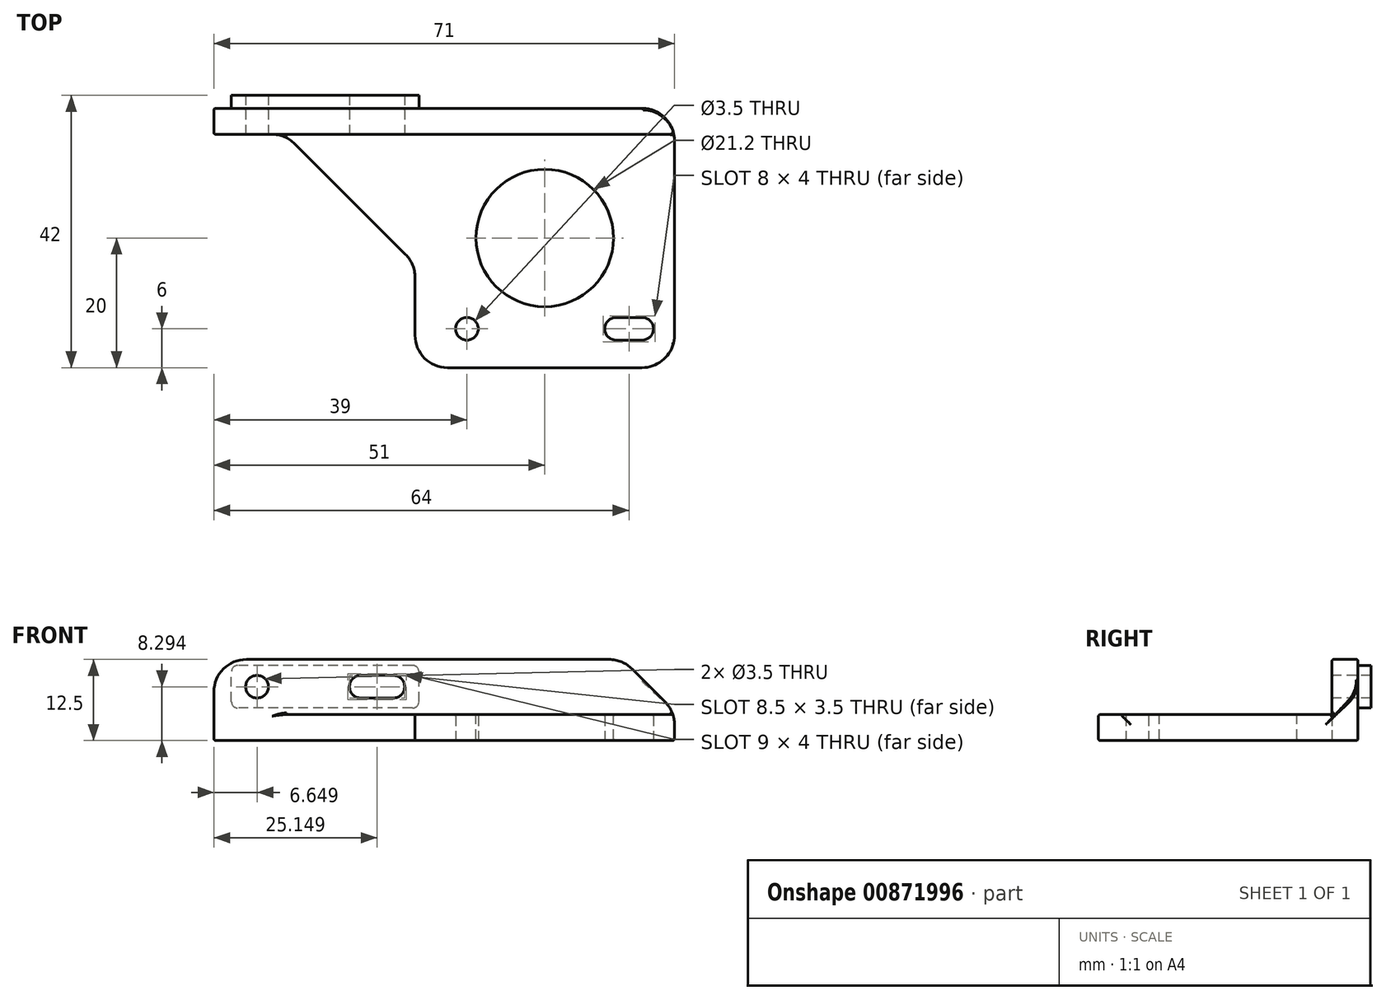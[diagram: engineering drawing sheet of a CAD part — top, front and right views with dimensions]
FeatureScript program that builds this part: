
annotation { "Feature Type Name" : "Feature", "Feature Type Description" : "" }
export const myFeature = defineFeature(function(context is Context, id is Id, definition is map)
    precondition{}
    {
        {
            var Q0;
            Q0=qCreatedBy(makeId("Top.planeOp"),FACE);
            var sketch = newSketch(context, id + "F0", { "sketchPlane" : qUnion([Q0])});
            skLineSegment(sketch, "E0.bottom", {"start": v(20, -20) * mm, "end": v(-20, -20) * mm});
            skLineSegment(sketch, "E0.top", {"start": v(20, 20) * mm, "end": v(-20, 20) * mm});
            skLineSegment(sketch, "E0.left", {"start": v(20, -20) * mm, "end": v(20, 20) * mm});
            skLineSegment(sketch, "E0.right", {"start": v(-20, -20) * mm, "end": v(-20, 20) * mm});
            skPoint(sketch, "E0.middle", {"position": v(0, 0) * mm});
            skCircle(sketch, "E1", {"center": v(-12, -14) * mm, "radius": 1.75 * mm});
            skLineSegment(sketch, "E2", {"start": v(11, -14) * mm, "end": v(15, -14) * mm});
            skArc(sketch, "E3.0.startCap", {"start": v(11, -15.75) * mm, "mid": v(9.25, -14) * mm, "end": v(11, -12.25) * mm});
            skArc(sketch, "E3.0.endCap", {"start": v(15, -12.25) * mm, "mid": v(16.75, -14) * mm, "end": v(15, -15.75) * mm});
            skLineSegment(sketch, "E3.0.left", {"start": v(11, -12.25) * mm, "end": v(15, -12.25) * mm});
            skLineSegment(sketch, "E3.0.right", {"start": v(11, -15.75) * mm, "end": v(15, -15.75) * mm});
            skSolve(sketch);
        }
        {
            var Q0;
            Q0 = qSketchRegion(id + "F0", true);
            extrude(context, id + "F1", {"entities" : qUnion([Q0]), "depth" : 4 * mm, "offsetDistance" : 25 * mm});
        }
        {
            var Q0;
            Q0=qCreatedBy(makeId("Top.planeOp"),FACE);
            var sketch = newSketch(context, id + "F2", { "sketchPlane" : qUnion([Q0])});
            skLineSegment(sketch, "E4.0", {"start": v(20, 20) * mm, "end": v(-20, 20) * mm, "construction": true});
            skLineSegment(sketch, "E5.bottom", {"start": v(20, 20) * mm, "end": v(-51, 20) * mm});
            skLineSegment(sketch, "E5.top", {"start": v(20, 16) * mm, "end": v(-51, 16) * mm});
            skLineSegment(sketch, "E5.left", {"start": v(20, 20) * mm, "end": v(20, 16) * mm});
            skLineSegment(sketch, "E5.right", {"start": v(-51, 20) * mm, "end": v(-51, 16) * mm});
            skSolve(sketch);
        }
        {
            var Q0;
            Q0 = qSketchRegion(id + "F2", true);
            extrude(context, id + "F3", {"entities" : qUnion([Q0]), "operationType" : NewBodyOperationType.ADD, "depth" : 12.5 * mm, "offsetDistance" : 25 * mm});
        }
        {
            var Q0;
            Q0=makeQuery(id+"F3.opExtrude","CAP_EDGE",EDGE,{"disambiguationData":[OSD([sQuery(id+"F2.wireOp",EDGE,"E5.left")])],"isStart":false});
            chamfer(context, id + "F4", {"entities" : qUnion([Q0]), "width" : 8 * mm, "tangentPropagation" : true});
        }
        {
            var Q0;
            Q0=makeQuery(id+"F3.opExtrude","SWEPT_FACE",FACE,{"disambiguationData":[OSD([sQuery(id+"F2.wireOp",EDGE,"E5.top")])]});
            var sketch = newSketch(context, id + "F5", { "sketchPlane" : qUnion([Q0])});
            skCircle(sketch, "E6", {"center": v(-44.35, 8.3) * mm, "radius": 1.75 * mm});
            skLineSegment(sketch, "E7", {"start": v(-28.35, 8.3) * mm, "end": v(-23.35, 8.3) * mm});
            skArc(sketch, "E8.0.startCap", {"start": v(-28.35, 6.54) * mm, "mid": v(-30.1, 8.3) * mm, "end": v(-28.35, 10.04) * mm});
            skArc(sketch, "E8.0.endCap", {"start": v(-23.35, 10.04) * mm, "mid": v(-21.6, 8.3) * mm, "end": v(-23.35, 6.54) * mm});
            skLineSegment(sketch, "E8.0.left", {"start": v(-28.35, 10.04) * mm, "end": v(-23.35, 10.04) * mm});
            skLineSegment(sketch, "E8.0.right", {"start": v(-28.35, 6.54) * mm, "end": v(-23.35, 6.54) * mm});
            skSolve(sketch);
        }
        {
            var Q0;
            Q0 = qSketchRegion(id + "F5", true);
            extrude(context, id + "F6", {"entities" : qUnion([Q0]), "operationType" : NewBodyOperationType.REMOVE, "endBound" : BoundingType.THROUGH_ALL, "oppositeDirection" : true, "depth" : 25 * mm, "offsetDistance" : 25 * mm});
        }
        {
            var Q0;
            Q0=makeQuery(id+"F3.boolean.opBoolean","INTERSECT",EDGE,{"derivedFrom":[makeQuery(id+"F1.opExtrude","SWEPT_FACE",FACE,{"disambiguationData":[OSD([sQuery(id+"F0.wireOp",EDGE,"E0.right")])]}),makeQuery(id+"F3.opExtrude","SWEPT_FACE",FACE,{"disambiguationData":[OSD([sQuery(id+"F2.wireOp",EDGE,"E5.top")])]})]});
            chamfer(context, id + "F7", {"entities" : qUnion([Q0]), "width" : 20 * mm, "tangentPropagation" : true});
        }
        {
            var Q0;
            Q0=makeQuery(id+"F3.boolean.opBoolean","MERGE",FACE,{"derivedFrom":[makeQuery(id+"F1.opExtrude","SWEPT_FACE",FACE,{"disambiguationData":[OSD([sQuery(id+"F0.wireOp",EDGE,"E0.top")])]}),makeQuery(id+"F3.opExtrude","SWEPT_FACE",FACE,{"disambiguationData":[OSD([sQuery(id+"F2.wireOp",EDGE,"E5.bottom")])]})]});
            var sketch = newSketch(context, id + "F8", { "sketchPlane" : qUnion([Q0])});
            skArc(sketch, "E9.0", {"start": v(28.35, 6.54) * mm, "mid": v(30.1, 8.3) * mm, "end": v(28.35, 10.04) * mm});
            skLineSegment(sketch, "E10.0", {"start": v(28.35, 6.54) * mm, "end": v(23.35, 6.54) * mm});
            skArc(sketch, "E11.0", {"start": v(23.35, 10.04) * mm, "mid": v(21.6, 8.3) * mm, "end": v(23.35, 6.54) * mm});
            skLineSegment(sketch, "E12.0", {"start": v(28.35, 10.04) * mm, "end": v(23.35, 10.04) * mm});
            skCircle(sketch, "E13.0", {"center": v(44.35, 8.3) * mm, "radius": 1.75 * mm});
            skLineSegment(sketch, "E14.0", {"start": v(40, 4) * mm, "end": v(-20, 4) * mm, "construction": true});
            skLineSegment(sketch, "E15.bottom", {"start": v(20.4, 5) * mm, "end": v(47.3, 5) * mm});
            skLineSegment(sketch, "E15.top", {"start": v(20.4, 11.59) * mm, "end": v(47.3, 11.59) * mm});
            skLineSegment(sketch, "E15.left", {"start": v(19.4, 6) * mm, "end": v(19.4, 10.59) * mm});
            skLineSegment(sketch, "E15.right", {"start": v(48.3, 6) * mm, "end": v(48.3, 10.59) * mm});
            skPoint(sketch, "E16.visualSharp", {"position": v(19.4, 11.59) * mm});
            skArc(sketch, "E16.filletArc", {"start": v(20.4, 11.59) * mm, "mid": v(19.7, 11.3) * mm, "end": v(19.4, 10.59) * mm});
            skPoint(sketch, "E17.visualSharp", {"position": v(19.4, 5) * mm});
            skArc(sketch, "E17.filletArc", {"start": v(19.4, 6) * mm, "mid": v(19.7, 5.3) * mm, "end": v(20.4, 5) * mm});
            skPoint(sketch, "E18.visualSharp", {"position": v(48.3, 5) * mm});
            skArc(sketch, "E18.filletArc", {"start": v(47.3, 5) * mm, "mid": v(48, 5.3) * mm, "end": v(48.3, 6) * mm});
            skPoint(sketch, "E19.visualSharp", {"position": v(48.3, 11.59) * mm});
            skArc(sketch, "E19.filletArc", {"start": v(48.3, 10.59) * mm, "mid": v(48, 11.3) * mm, "end": v(47.3, 11.59) * mm});
            skSolve(sketch);
        }
        {
            var Q0;
            Q0 = qSketchRegion(id + "F8", true);
            extrude(context, id + "F9", {"entities" : qUnion([Q0]), "depth" : 2 * mm, "offsetDistance" : 25 * mm});
        }
        {
            var Q0;
            Q0=makeQuery(id+"F1.opExtrude","CAP_FACE",FACE,{"disambiguationData":[OSD([sQuery(id+"F0.wireOp",EDGE,"E0.bottom"),sQuery(id+"F0.wireOp",EDGE,"E0.top"),sQuery(id+"F0.wireOp",EDGE,"E0.left"),sQuery(id+"F0.wireOp",EDGE,"E0.right"),sQuery(id+"F0.wireOp",EDGE,"E1"),sQuery(id+"F0.wireOp",EDGE,"E3.0.startCap"),sQuery(id+"F0.wireOp",EDGE,"E3.0.endCap"),sQuery(id+"F0.wireOp",EDGE,"E3.0.left"),sQuery(id+"F0.wireOp",EDGE,"E3.0.right")])],"isStart":false});
            var sketch = newSketch(context, id + "F10", { "sketchPlane" : qUnion([Q0])});
            skCircle(sketch, "E20", {"center": v(0, 0) * mm, "radius": 10.6 * mm});
            skSolve(sketch);
        }
        {
            var Q0;
            Q0 = qSketchRegion(id + "F10", true);
            extrude(context, id + "F11", {"entities" : qUnion([Q0]), "operationType" : NewBodyOperationType.REMOVE, "oppositeDirection" : true, "depth" : 25 * mm, "offsetDistance" : 25 * mm});
        }
        {
            var Q0;
            Q0=makeQuery(id+"F1.opExtrude","SWEPT_EDGE",EDGE,{"disambiguationData":[OSD([sQuery(id+"F0.wireOp",EDGE,"E0.bottom"),sQuery(id+"F0.wireOp",EDGE,"E0.right")])]});
            var Q1;
            Q1=makeQuery(id+"F1.opExtrude","SWEPT_EDGE",EDGE,{"disambiguationData":[OSD([sQuery(id+"F0.wireOp",EDGE,"E0.bottom"),sQuery(id+"F0.wireOp",EDGE,"E0.left")])]});
            var Q2;
            Q2=makeQuery(id+"F3.boolean.opBoolean","MERGE",EDGE,{"derivedFrom":[makeQuery(id+"F1.opExtrude","SWEPT_EDGE",EDGE,{"disambiguationData":[OSD([sQuery(id+"F0.wireOp",EDGE,"E0.top"),sQuery(id+"F0.wireOp",EDGE,"E0.left")])]}),makeQuery(id+"F3.opExtrude","SWEPT_EDGE",EDGE,{"disambiguationData":[OSD([sQuery(id+"F2.wireOp",EDGE,"E5.bottom"),sQuery(id+"F2.wireOp",EDGE,"E5.left")])]})]});
            var Q3;
            {var subQ0=sQuery(id+"F2.wireOp",EDGE,"E5.left");Q3=makeQuery(id+"F4.opChamfer","BLEND_EDGE",EDGE,{"blendedFrom":[makeQuery(id+"F3.opExtrude","CAP_EDGE",EDGE,{"disambiguationData":[OSD([subQ0])],"isStart":false}),makeQuery(id+"F3.opExtrude","CAP_FACE",FACE,{"disambiguationData":[OSD([sQuery(id+"F2.wireOp",EDGE,"E5.bottom"),sQuery(id+"F2.wireOp",EDGE,"E5.top"),subQ0,sQuery(id+"F2.wireOp",EDGE,"E5.right")])],"isStart":false})],"blendedInto":[makeQuery(id+"F3.opExtrude","CAP_FACE",FACE,{"disambiguationData":[OSD([sQuery(id+"F2.wireOp",EDGE,"E5.bottom"),sQuery(id+"F2.wireOp",EDGE,"E5.top"),subQ0,sQuery(id+"F2.wireOp",EDGE,"E5.right")])],"isStart":false})]});}
            var Q4;
            {var subQ0=sQuery(id+"F2.wireOp",EDGE,"E5.left");Q4=makeQuery(id+"F4.opChamfer","BLEND_EDGE",EDGE,{"blendedFrom":[makeQuery(id+"F3.opExtrude","CAP_EDGE",EDGE,{"disambiguationData":[OSD([subQ0])],"isStart":false}),makeQuery(id+"F3.boolean.opBoolean","MERGE",FACE,{"derivedFrom":[makeQuery(id+"F1.opExtrude","SWEPT_FACE",FACE,{"disambiguationData":[OSD([sQuery(id+"F0.wireOp",EDGE,"E0.left")])]}),makeQuery(id+"F3.opExtrude","SWEPT_FACE",FACE,{"disambiguationData":[OSD([subQ0])]})]})],"blendedInto":[makeQuery(id+"F3.boolean.opBoolean","MERGE",FACE,{"derivedFrom":[makeQuery(id+"F1.opExtrude","SWEPT_FACE",FACE,{"disambiguationData":[OSD([sQuery(id+"F0.wireOp",EDGE,"E0.left")])]}),makeQuery(id+"F3.opExtrude","SWEPT_FACE",FACE,{"disambiguationData":[OSD([subQ0])]})]})]});}
            var Q5;
            {var subQ0=makeQuery(id+"F1.opExtrude","SWEPT_FACE",FACE,{"disambiguationData":[OSD([sQuery(id+"F0.wireOp",EDGE,"E0.right")])]});Q5=makeQuery(id+"F7.opChamfer","BLEND_EDGE",EDGE,{"blendedFrom":[makeQuery(id+"F3.boolean.opBoolean","INTERSECT",EDGE,{"derivedFrom":[subQ0,makeQuery(id+"F3.opExtrude","SWEPT_FACE",FACE,{"disambiguationData":[OSD([sQuery(id+"F2.wireOp",EDGE,"E5.top")])]})]}),subQ0],"blendedInto":[subQ0]});}
            var Q6;
            {var subQ0=makeQuery(id+"F3.opExtrude","SWEPT_FACE",FACE,{"disambiguationData":[OSD([sQuery(id+"F2.wireOp",EDGE,"E5.top")])]});Q6=makeQuery(id+"F7.opChamfer","BLEND_EDGE",EDGE,{"blendedFrom":[makeQuery(id+"F3.boolean.opBoolean","INTERSECT",EDGE,{"derivedFrom":[makeQuery(id+"F1.opExtrude","SWEPT_FACE",FACE,{"disambiguationData":[OSD([sQuery(id+"F0.wireOp",EDGE,"E0.right")])]}),subQ0]}),subQ0],"blendedInto":[subQ0]});}
            fillet(context, id + "F12", {"entities" : qUnion([Q0, Q1, Q2, Q3, Q4, Q5, Q6]), "radius" : 5 * mm, "tangentPropagation" : true, "allowEdgeOverflow" : false});
        }
        {
            var Q0;
            Q0=makeQuery(id+"F3.opExtrude","SWEPT_FACE",FACE,{"disambiguationData":[OSD([sQuery(id+"F2.wireOp",EDGE,"E5.top")])]});
            var Q1;
            Q1=makeQuery(id+"F1.opExtrude","CAP_FACE",FACE,{"disambiguationData":[OSD([sQuery(id+"F0.wireOp",EDGE,"E0.bottom"),sQuery(id+"F0.wireOp",EDGE,"E0.top"),sQuery(id+"F0.wireOp",EDGE,"E0.left"),sQuery(id+"F0.wireOp",EDGE,"E0.right"),sQuery(id+"F0.wireOp",EDGE,"E1"),sQuery(id+"F0.wireOp",EDGE,"E3.0.startCap"),sQuery(id+"F0.wireOp",EDGE,"E3.0.endCap"),sQuery(id+"F0.wireOp",EDGE,"E3.0.left"),sQuery(id+"F0.wireOp",EDGE,"E3.0.right")])],"isStart":false});
            var Q2;
            Q2=makeQuery(id+"F3.boolean.opBoolean","MERGE",FACE,{"derivedFrom":[makeQuery(id+"F1.opExtrude","SWEPT_FACE",FACE,{"disambiguationData":[OSD([sQuery(id+"F0.wireOp",EDGE,"E0.top")])]}),makeQuery(id+"F3.opExtrude","SWEPT_FACE",FACE,{"disambiguationData":[OSD([sQuery(id+"F2.wireOp",EDGE,"E5.bottom")])]})]});
            var Q3;
            Q3=makeQuery(id+"F3.boolean.opBoolean","MERGE",FACE,{"derivedFrom":[makeQuery(id+"F1.opExtrude","CAP_FACE",FACE,{"disambiguationData":[OSD([sQuery(id+"F0.wireOp",EDGE,"E0.bottom"),sQuery(id+"F0.wireOp",EDGE,"E0.top"),sQuery(id+"F0.wireOp",EDGE,"E0.left"),sQuery(id+"F0.wireOp",EDGE,"E0.right"),sQuery(id+"F0.wireOp",EDGE,"E1"),sQuery(id+"F0.wireOp",EDGE,"E3.0.startCap"),sQuery(id+"F0.wireOp",EDGE,"E3.0.endCap"),sQuery(id+"F0.wireOp",EDGE,"E3.0.left"),sQuery(id+"F0.wireOp",EDGE,"E3.0.right")])],"isStart":true}),makeQuery(id+"F3.opExtrude","CAP_FACE",FACE,{"disambiguationData":[OSD([sQuery(id+"F2.wireOp",EDGE,"E5.bottom"),sQuery(id+"F2.wireOp",EDGE,"E5.top"),sQuery(id+"F2.wireOp",EDGE,"E5.left"),sQuery(id+"F2.wireOp",EDGE,"E5.right")])],"isStart":true})]});
            fillet(context, id + "F13", {"entities" : qUnion([Q0, Q1, Q2, Q3]), "radius" : .25 * mm, "tangentPropagation" : true, "allowEdgeOverflow" : false});
        }
        {
            var Q0;
            Q0=makeQuery(id+"F3.opExtrude","CAP_EDGE",EDGE,{"disambiguationData":[OSD([sQuery(id+"F2.wireOp",EDGE,"E5.right")])],"isStart":false});
            fillet(context, id + "F14", {"entities" : qUnion([Q0]), "radius" : 5 * mm, "tangentPropagation" : true, "allowEdgeOverflow" : false});
        }
    });
